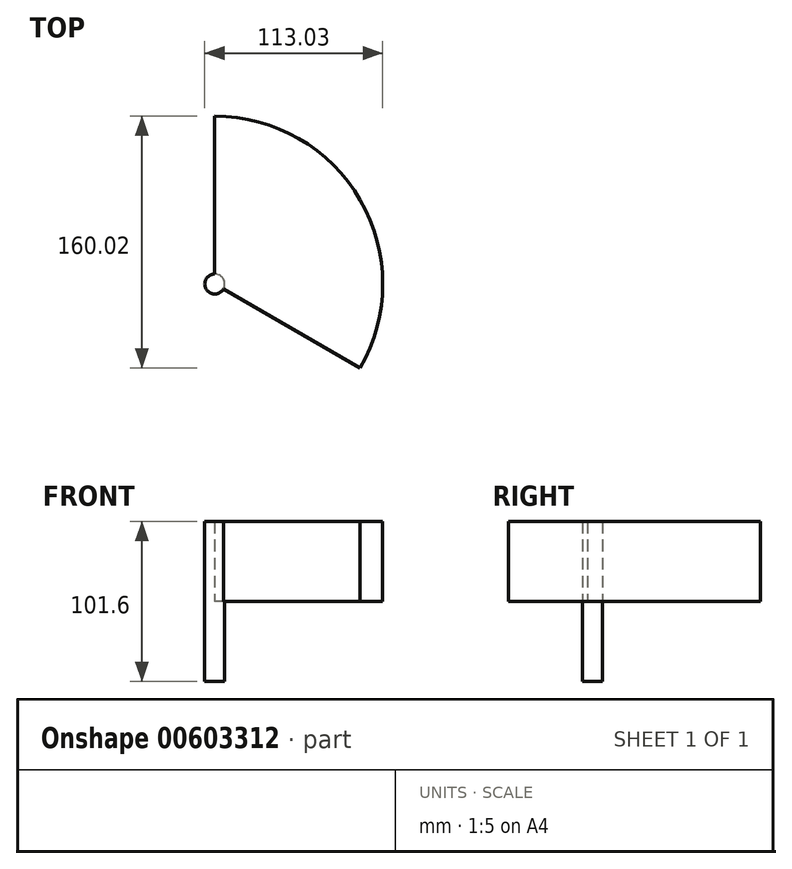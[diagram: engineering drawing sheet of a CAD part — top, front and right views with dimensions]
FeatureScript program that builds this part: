
annotation { "Feature Type Name" : "Feature", "Feature Type Description" : "" }
export const myFeature = defineFeature(function(context is Context, id is Id, definition is map)
    precondition{}
    {
        {
            var Q0;
            Q0=qCreatedBy(makeId("Top.planeOp"),FACE);
            var sketch = newSketch(context, id + "F0", { "sketchPlane" : qUnion([Q0])});
            skLineSegment(sketch, "E0", {"start": v(0, 0) * mm, "end": v(0, 106.68) * mm});
            skLineSegment(sketch, "E1", {"start": v(0, 0) * mm, "end": v(92.39, -53.34) * mm});
            skArc(sketch, "E2", {"start": v(0, 106.68) * mm, "mid": v(92.39, 53.34) * mm, "end": v(92.39, -53.34) * mm});
            skSolve(sketch);
        }
        {
            var Q0;
            Q0=makeQuery(id+"F0.imprint","IMPRINT",FACE,{"disambiguationData":[TD([[makeQuery(id+"F0.imprint","IMPRINT",EDGE,{"derivedFrom":sQuery(id+"F0.wireOp",EDGE,"E0")}),-1.0]])]});
            extrude(context, id + "F1", {"entities" : qUnion([Q0]), "depth" : 50.8 * mm, "offsetDistance" : 25.4 * mm});
        }
        {
            var Q0;
            Q0=qCreatedBy(makeId("Top.planeOp"),FACE);
            var sketch = newSketch(context, id + "F2", { "sketchPlane" : qUnion([Q0])});
            skCircle(sketch, "E3", {"center": v(0, 0) * mm, "radius": 6.35 * mm});
            skSolve(sketch);
        }
        {
            var Q0;
            Q0=makeQuery(id+"F2.imprint","IMPRINT",FACE,{"disambiguationData":[TD([[makeQuery(id+"F2.imprint","IMPRINT",EDGE,{"derivedFrom":sQuery(id+"F2.wireOp",EDGE,"E3")}),1.0]])]});
            var Q1;
            Q1=sQuery(id+"F2.wireOp",EDGE,"E3");
            extrude(context, id + "F3", {"entities" : qUnion([Q0]), "surfaceEntities" : qUnion([Q1]), "depth" : 50.8 * mm, "offsetDistance" : 25.4 * mm});
        }
        {
            var Q0;
            Q0 = qSketchRegion(id + "F2", true);
            extrude(context, id + "F4", {"entities" : qUnion([Q0]), "operationType" : NewBodyOperationType.ADD, "oppositeDirection" : true, "depth" : 50.8 * mm, "offsetDistance" : 25.4 * mm});
        }
    });
